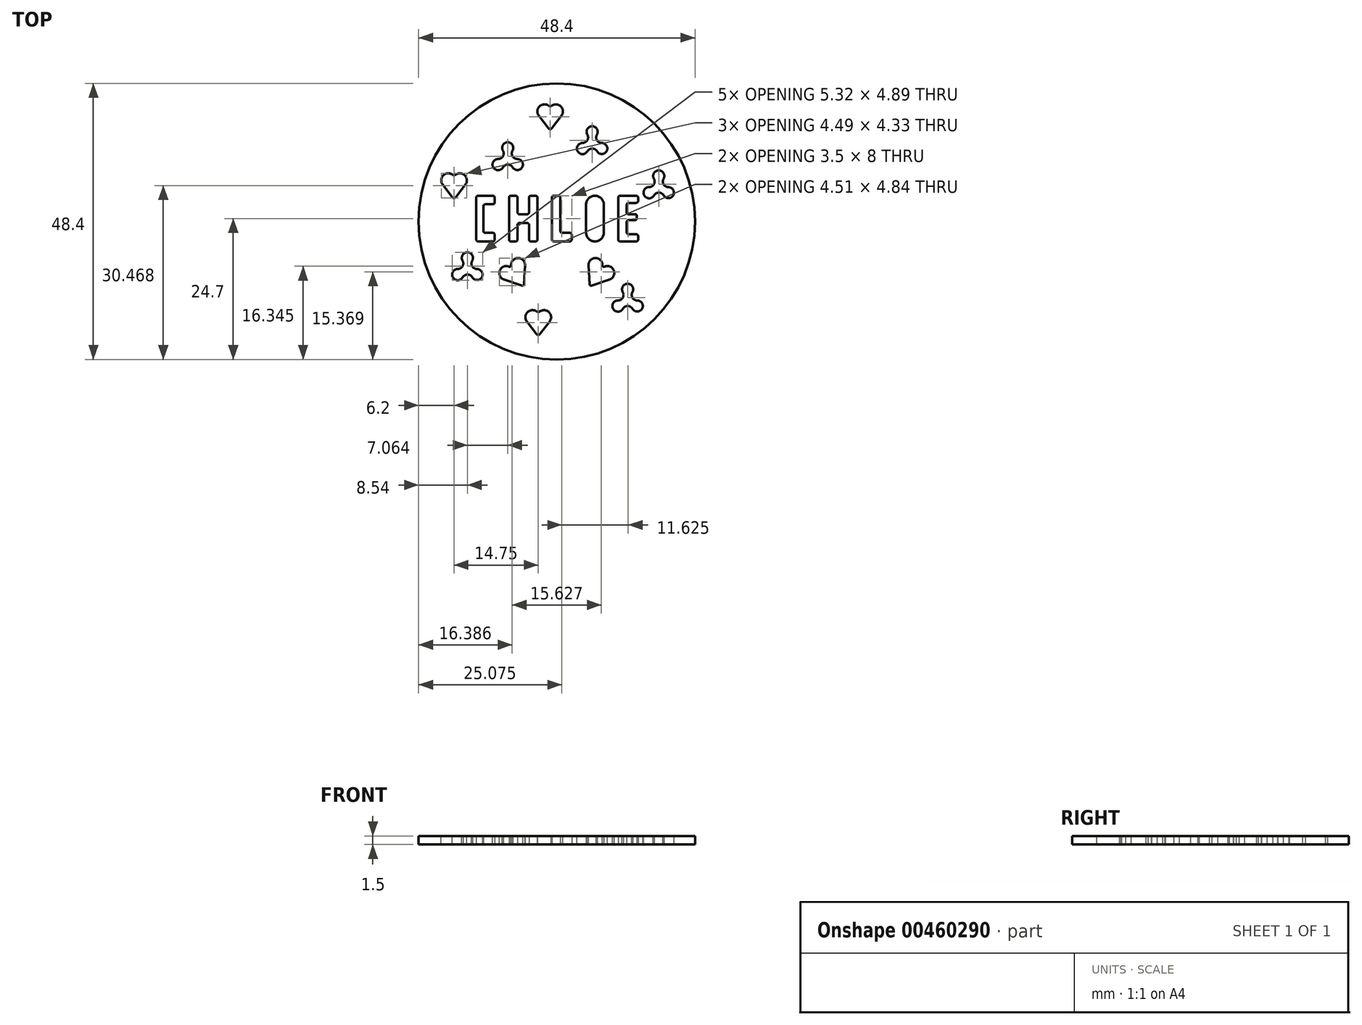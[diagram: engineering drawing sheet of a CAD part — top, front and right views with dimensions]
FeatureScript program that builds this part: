
annotation { "Feature Type Name" : "Feature", "Feature Type Description" : "" }
export const myFeature = defineFeature(function(context is Context, id is Id, definition is map)
    precondition{}
    {
        {
            var Q0;
            Q0=qCreatedBy(makeId("Top.planeOp"),FACE);
            var sketch = newSketch(context, id + "F0", { "sketchPlane" : qUnion([Q0])});
            skCircle(sketch, "E0", {"center": v(0, 0) * mm, "radius": 24.2 * mm});
            skLineSegment(sketch, "E1", {"start": v(-14.12, 4.15) * mm, "end": v(-14.12, -3.15) * mm});
            skLineSegment(sketch, "E2", {"start": v(-13.77, -3.5) * mm, "end": v(-11.22, -3.5) * mm});
            skLineSegment(sketch, "E3", {"start": v(-13.77, 4.5) * mm, "end": v(-11.22, 4.5) * mm});
            skLineSegment(sketch, "E4", {"start": v(-8.37, 4.15) * mm, "end": v(-8.37, -3.15) * mm});
            skLineSegment(sketch, "E5", {"start": v(-8.02, -3.5) * mm, "end": v(-7.22, -3.5) * mm});
            skLineSegment(sketch, "E6", {"start": v(-6.87, -3.15) * mm, "end": v(-6.87, -0.6) * mm});
            skLineSegment(sketch, "E7", {"start": v(-6.52, -0.25) * mm, "end": v(-5.22, -0.25) * mm});
            skLineSegment(sketch, "E8", {"start": v(-4.87, -0.6) * mm, "end": v(-4.87, -3.15) * mm});
            skLineSegment(sketch, "E9", {"start": v(-4.53, -3.5) * mm, "end": v(-3.73, -3.5) * mm});
            skLineSegment(sketch, "E10", {"start": v(-3.38, -3.15) * mm, "end": v(-3.38, 4.15) * mm});
            skLineSegment(sketch, "E11", {"start": v(-3.73, 4.5) * mm, "end": v(-4.52, 4.5) * mm});
            skLineSegment(sketch, "E12", {"start": v(-4.87, 4.15) * mm, "end": v(-4.87, 1.6) * mm});
            skLineSegment(sketch, "E13", {"start": v(-5.22, 1.25) * mm, "end": v(-6.52, 1.25) * mm});
            skLineSegment(sketch, "E14", {"start": v(-6.87, 1.6) * mm, "end": v(-6.87, 4.15) * mm});
            skLineSegment(sketch, "E15", {"start": v(-7.22, 4.5) * mm, "end": v(-8.02, 4.5) * mm});
            skLineSegment(sketch, "E16", {"start": v(-0.88, 4.15) * mm, "end": v(-0.87, -3.15) * mm});
            skLineSegment(sketch, "E17", {"start": v(-0.52, -3.5) * mm, "end": v(2.28, -3.5) * mm});
            skLineSegment(sketch, "E18", {"start": v(2.63, -3.15) * mm, "end": v(2.63, -2.35) * mm});
            skLineSegment(sketch, "E19", {"start": v(2.28, -2) * mm, "end": v(0.98, -2) * mm});
            skLineSegment(sketch, "E20", {"start": v(0.63, -1.65) * mm, "end": v(0.62, 4.15) * mm});
            skLineSegment(sketch, "E21", {"start": v(0.27, 4.5) * mm, "end": v(-0.53, 4.5) * mm});
            skLineSegment(sketch, "E22", {"start": v(5.12, 2.94) * mm, "end": v(5.13, -1.94) * mm});
            skLineSegment(sketch, "E23", {"start": v(8.25, 2.94) * mm, "end": v(8.25, -1.94) * mm});
            skArc(sketch, "E24", {"start": v(5.12, 2.94) * mm, "mid": v(6.69, 4.5) * mm, "end": v(8.25, 2.94) * mm});
            skArc(sketch, "E25", {"start": v(8.25, -1.94) * mm, "mid": v(6.69, -3.5) * mm, "end": v(5.12, -1.94) * mm});
            skLineSegment(sketch, "E26", {"start": v(13.9, 4.5) * mm, "end": v(11.1, 4.5) * mm});
            skLineSegment(sketch, "E27", {"start": v(10.75, 4.15) * mm, "end": v(10.75, -3.15) * mm});
            skLineSegment(sketch, "E28", {"start": v(11.1, -3.5) * mm, "end": v(13.9, -3.5) * mm});
            skLineSegment(sketch, "E29", {"start": v(14.25, -3.15) * mm, "end": v(14.25, -2.6) * mm});
            skLineSegment(sketch, "E30", {"start": v(13.9, -2.25) * mm, "end": v(12.6, -2.25) * mm});
            skLineSegment(sketch, "E31", {"start": v(12.25, -1.9) * mm, "end": v(12.25, -0.1) * mm});
            skLineSegment(sketch, "E32", {"start": v(14, 0.5) * mm, "end": v(14, 1) * mm});
            skLineSegment(sketch, "E33", {"start": v(13.75, 1.25) * mm, "end": v(12.6, 1.25) * mm});
            skLineSegment(sketch, "E34", {"start": v(12.25, 1.6) * mm, "end": v(12.25, 2.9) * mm});
            skLineSegment(sketch, "E35", {"start": v(12.6, 3.25) * mm, "end": v(13.9, 3.25) * mm});
            skLineSegment(sketch, "E36", {"start": v(14.25, 3.6) * mm, "end": v(14.25, 4.15) * mm});
            skLineSegment(sketch, "E37", {"start": v(-10.87, 4.15) * mm, "end": v(-10.87, 3.35) * mm});
            skLineSegment(sketch, "E38", {"start": v(-11.22, 3) * mm, "end": v(-12.52, 3) * mm});
            skLineSegment(sketch, "E39", {"start": v(-12.87, 2.65) * mm, "end": v(-12.87, -1.65) * mm});
            skLineSegment(sketch, "E40", {"start": v(-12.52, -2) * mm, "end": v(-11.22, -2) * mm});
            skLineSegment(sketch, "E41", {"start": v(-10.87, -2.35) * mm, "end": v(-10.87, -3.15) * mm});
            skPoint(sketch, "E42.visualSharp", {"position": v(-14.12, 4.5) * mm});
            skArc(sketch, "E42.filletArc", {"start": v(-13.77, 4.5) * mm, "mid": v(-14.02, 4.4) * mm, "end": v(-14.12, 4.15) * mm});
            skPoint(sketch, "E43.visualSharp", {"position": v(-10.87, 4.5) * mm});
            skArc(sketch, "E43.filletArc", {"start": v(-10.87, 4.15) * mm, "mid": v(-10.98, 4.4) * mm, "end": v(-11.22, 4.5) * mm});
            skPoint(sketch, "E44.visualSharp", {"position": v(-10.87, 3) * mm});
            skArc(sketch, "E44.filletArc", {"start": v(-11.22, 3) * mm, "mid": v(-10.98, 3.1) * mm, "end": v(-10.87, 3.35) * mm});
            skPoint(sketch, "E45.visualSharp", {"position": v(-12.87, 3) * mm});
            skArc(sketch, "E45.filletArc", {"start": v(-12.52, 3) * mm, "mid": v(-12.77, 2.9) * mm, "end": v(-12.87, 2.65) * mm});
            skPoint(sketch, "E46.visualSharp", {"position": v(-12.87, -2) * mm});
            skArc(sketch, "E46.filletArc", {"start": v(-12.87, -1.65) * mm, "mid": v(-12.77, -1.9) * mm, "end": v(-12.52, -2) * mm});
            skPoint(sketch, "E47.visualSharp", {"position": v(-10.87, -2) * mm});
            skArc(sketch, "E47.filletArc", {"start": v(-10.87, -2.35) * mm, "mid": v(-10.98, -2.1) * mm, "end": v(-11.22, -2) * mm});
            skPoint(sketch, "E48.visualSharp", {"position": v(-10.87, -3.5) * mm});
            skArc(sketch, "E48.filletArc", {"start": v(-11.22, -3.5) * mm, "mid": v(-10.98, -3.4) * mm, "end": v(-10.87, -3.15) * mm});
            skPoint(sketch, "E49.visualSharp", {"position": v(-14.12, -3.5) * mm});
            skArc(sketch, "E49.filletArc", {"start": v(-14.12, -3.15) * mm, "mid": v(-14.02, -3.4) * mm, "end": v(-13.77, -3.5) * mm});
            skPoint(sketch, "E50.visualSharp", {"position": v(-8.37, 4.5) * mm});
            skArc(sketch, "E50.filletArc", {"start": v(-8.02, 4.5) * mm, "mid": v(-8.27, 4.4) * mm, "end": v(-8.37, 4.15) * mm});
            skPoint(sketch, "E51.visualSharp", {"position": v(-6.87, 4.5) * mm});
            skArc(sketch, "E51.filletArc", {"start": v(-6.87, 4.15) * mm, "mid": v(-6.98, 4.4) * mm, "end": v(-7.22, 4.5) * mm});
            skPoint(sketch, "E52.visualSharp", {"position": v(-6.87, 1.25) * mm});
            skArc(sketch, "E52.filletArc", {"start": v(-6.87, 1.6) * mm, "mid": v(-6.77, 1.35) * mm, "end": v(-6.52, 1.25) * mm});
            skPoint(sketch, "E53.visualSharp", {"position": v(-4.87, 1.25) * mm});
            skArc(sketch, "E53.filletArc", {"start": v(-5.22, 1.25) * mm, "mid": v(-4.98, 1.35) * mm, "end": v(-4.87, 1.6) * mm});
            skPoint(sketch, "E54.visualSharp", {"position": v(-4.87, 4.5) * mm});
            skArc(sketch, "E54.filletArc", {"start": v(-4.52, 4.5) * mm, "mid": v(-4.77, 4.4) * mm, "end": v(-4.87, 4.15) * mm});
            skPoint(sketch, "E55.visualSharp", {"position": v(-3.38, 4.5) * mm});
            skArc(sketch, "E55.filletArc", {"start": v(-3.37, 4.15) * mm, "mid": v(-3.48, 4.4) * mm, "end": v(-3.73, 4.5) * mm});
            skPoint(sketch, "E56.visualSharp", {"position": v(-3.37, -3.5) * mm});
            skArc(sketch, "E56.filletArc", {"start": v(-3.73, -3.5) * mm, "mid": v(-3.48, -3.4) * mm, "end": v(-3.37, -3.15) * mm});
            skPoint(sketch, "E57.visualSharp", {"position": v(-4.87, -3.5) * mm});
            skArc(sketch, "E57.filletArc", {"start": v(-4.88, -3.15) * mm, "mid": v(-4.77, -3.4) * mm, "end": v(-4.53, -3.5) * mm});
            skPoint(sketch, "E58.visualSharp", {"position": v(-4.87, -0.25) * mm});
            skArc(sketch, "E58.filletArc", {"start": v(-4.87, -0.6) * mm, "mid": v(-4.98, -0.35) * mm, "end": v(-5.22, -0.25) * mm});
            skPoint(sketch, "E59.visualSharp", {"position": v(-6.87, -0.25) * mm});
            skArc(sketch, "E59.filletArc", {"start": v(-6.52, -0.25) * mm, "mid": v(-6.77, -0.35) * mm, "end": v(-6.87, -0.6) * mm});
            skPoint(sketch, "E60.visualSharp", {"position": v(-6.87, -3.5) * mm});
            skArc(sketch, "E60.filletArc", {"start": v(-7.22, -3.5) * mm, "mid": v(-6.98, -3.4) * mm, "end": v(-6.87, -3.15) * mm});
            skPoint(sketch, "E61.visualSharp", {"position": v(-8.37, -3.5) * mm});
            skArc(sketch, "E61.filletArc", {"start": v(-8.37, -3.15) * mm, "mid": v(-8.27, -3.4) * mm, "end": v(-8.02, -3.5) * mm});
            skPoint(sketch, "E62.visualSharp", {"position": v(-0.88, 4.5) * mm});
            skArc(sketch, "E62.filletArc", {"start": v(-0.53, 4.5) * mm, "mid": v(-0.77, 4.4) * mm, "end": v(-0.88, 4.15) * mm});
            skPoint(sketch, "E63.visualSharp", {"position": v(0.62, 4.5) * mm});
            skArc(sketch, "E63.filletArc", {"start": v(0.62, 4.15) * mm, "mid": v(0.52, 4.4) * mm, "end": v(0.27, 4.5) * mm});
            skPoint(sketch, "E64.visualSharp", {"position": v(0.63, -2) * mm});
            skArc(sketch, "E64.filletArc", {"start": v(0.63, -1.65) * mm, "mid": v(0.73, -1.9) * mm, "end": v(0.98, -2) * mm});
            skPoint(sketch, "E65.visualSharp", {"position": v(2.63, -2) * mm});
            skArc(sketch, "E65.filletArc", {"start": v(2.63, -2.35) * mm, "mid": v(2.52, -2.1) * mm, "end": v(2.28, -2) * mm});
            skPoint(sketch, "E66.visualSharp", {"position": v(2.63, -3.5) * mm});
            skArc(sketch, "E66.filletArc", {"start": v(2.28, -3.5) * mm, "mid": v(2.52, -3.4) * mm, "end": v(2.63, -3.15) * mm});
            skPoint(sketch, "E67.visualSharp", {"position": v(-0.87, -3.5) * mm});
            skArc(sketch, "E67.filletArc", {"start": v(-0.87, -3.15) * mm, "mid": v(-0.77, -3.4) * mm, "end": v(-0.52, -3.5) * mm});
            skPoint(sketch, "E68.visualSharp", {"position": v(14.25, -3.5) * mm});
            skArc(sketch, "E68.filletArc", {"start": v(13.9, -3.5) * mm, "mid": v(14.15, -3.4) * mm, "end": v(14.25, -3.15) * mm});
            skPoint(sketch, "E69.visualSharp", {"position": v(14.25, -2.25) * mm});
            skArc(sketch, "E69.filletArc", {"start": v(14.25, -2.6) * mm, "mid": v(14.15, -2.35) * mm, "end": v(13.9, -2.25) * mm});
            skPoint(sketch, "E70.visualSharp", {"position": v(12.25, -2.25) * mm});
            skArc(sketch, "E70.filletArc", {"start": v(12.25, -1.9) * mm, "mid": v(12.35, -2.15) * mm, "end": v(12.6, -2.25) * mm});
            skPoint(sketch, "E71.visualSharp", {"position": v(12.25, 0) * mm});
            skArc(sketch, "E71.filletArc", {"start": v(12.6, 0.25) * mm, "mid": v(12.35, 0.15) * mm, "end": v(12.25, -0.1) * mm});
            skPoint(sketch, "E72.visualSharp", {"position": v(10.75, -3.5) * mm});
            skArc(sketch, "E72.filletArc", {"start": v(10.75, -3.15) * mm, "mid": v(10.85, -3.4) * mm, "end": v(11.1, -3.5) * mm});
            skPoint(sketch, "E73.visualSharp", {"position": v(10.75, 4.5) * mm});
            skArc(sketch, "E73.filletArc", {"start": v(11.1, 4.5) * mm, "mid": v(10.85, 4.4) * mm, "end": v(10.75, 4.15) * mm});
            skPoint(sketch, "E74.visualSharp", {"position": v(14.25, 4.5) * mm});
            skArc(sketch, "E74.filletArc", {"start": v(14.25, 4.15) * mm, "mid": v(14.15, 4.4) * mm, "end": v(13.9, 4.5) * mm});
            skPoint(sketch, "E75.visualSharp", {"position": v(14.25, 3.25) * mm});
            skArc(sketch, "E75.filletArc", {"start": v(13.9, 3.25) * mm, "mid": v(14.15, 3.35) * mm, "end": v(14.25, 3.6) * mm});
            skPoint(sketch, "E76.visualSharp", {"position": v(12.25, 3.25) * mm});
            skArc(sketch, "E76.filletArc", {"start": v(12.6, 3.25) * mm, "mid": v(12.35, 3.15) * mm, "end": v(12.25, 2.9) * mm});
            skPoint(sketch, "E77.visualSharp", {"position": v(12.25, 1.25) * mm});
            skArc(sketch, "E77.filletArc", {"start": v(12.25, 1.6) * mm, "mid": v(12.35, 1.35) * mm, "end": v(12.6, 1.25) * mm});
            skPoint(sketch, "E78.visualSharp", {"position": v(14, 1.25) * mm});
            skArc(sketch, "E78.filletArc", {"start": v(14, 1) * mm, "mid": v(13.93, 1.18) * mm, "end": v(13.75, 1.25) * mm});
            skArc(sketch, "E79.filletArc", {"start": v(13.75, 0.25) * mm, "mid": v(13.93, 0.32) * mm, "end": v(14, 0.5) * mm});
            skLineSegment(sketch, "E80", {"start": v(13.75, 0.25) * mm, "end": v(12.6, 0.25) * mm});
            skSolve(sketch);
        }
        {
            var Q0;
            Q0 = qSketchRegion(id + "F0", true);
            extrude(context, id + "F1", {"entities" : qUnion([Q0]), "depth" : 1.5 * mm});
        }
        {
            var Q0;
            Q0=makeQuery(id+"F1.opExtrude","CAP_FACE",FACE,{"disambiguationData":[OSD([sQuery(id+"F0.wireOp",EDGE,"E0"),sQuery(id+"F0.wireOp",EDGE,"E1"),sQuery(id+"F0.wireOp",EDGE,"E2"),sQuery(id+"F0.wireOp",EDGE,"E3"),sQuery(id+"F0.wireOp",EDGE,"E4"),sQuery(id+"F0.wireOp",EDGE,"E5"),sQuery(id+"F0.wireOp",EDGE,"E6"),sQuery(id+"F0.wireOp",EDGE,"E7"),sQuery(id+"F0.wireOp",EDGE,"E8"),sQuery(id+"F0.wireOp",EDGE,"E9"),sQuery(id+"F0.wireOp",EDGE,"E10"),sQuery(id+"F0.wireOp",EDGE,"E11"),sQuery(id+"F0.wireOp",EDGE,"E12"),sQuery(id+"F0.wireOp",EDGE,"E13"),sQuery(id+"F0.wireOp",EDGE,"E14"),sQuery(id+"F0.wireOp",EDGE,"E15"),sQuery(id+"F0.wireOp",EDGE,"E16"),sQuery(id+"F0.wireOp",EDGE,"E17"),sQuery(id+"F0.wireOp",EDGE,"E18"),sQuery(id+"F0.wireOp",EDGE,"E19"),sQuery(id+"F0.wireOp",EDGE,"E20"),sQuery(id+"F0.wireOp",EDGE,"E21"),sQuery(id+"F0.wireOp",EDGE,"E22"),sQuery(id+"F0.wireOp",EDGE,"E23"),sQuery(id+"F0.wireOp",EDGE,"E24"),sQuery(id+"F0.wireOp",EDGE,"E25"),sQuery(id+"F0.wireOp",EDGE,"E26"),sQuery(id+"F0.wireOp",EDGE,"E27"),sQuery(id+"F0.wireOp",EDGE,"E28"),sQuery(id+"F0.wireOp",EDGE,"E29"),sQuery(id+"F0.wireOp",EDGE,"E30"),sQuery(id+"F0.wireOp",EDGE,"E31"),sQuery(id+"F0.wireOp",EDGE,"e08n0Kjc-3YKp-OetY-h4IO-rFLRSXg9Mj5R"),sQuery(id+"F0.wireOp",EDGE,"E32"),sQuery(id+"F0.wireOp",EDGE,"E33"),sQuery(id+"F0.wireOp",EDGE,"E34"),sQuery(id+"F0.wireOp",EDGE,"E35"),sQuery(id+"F0.wireOp",EDGE,"E36"),sQuery(id+"F0.wireOp",EDGE,"E37"),sQuery(id+"F0.wireOp",EDGE,"E38"),sQuery(id+"F0.wireOp",EDGE,"E39"),sQuery(id+"F0.wireOp",EDGE,"E40"),sQuery(id+"F0.wireOp",EDGE,"E41"),sQuery(id+"F0.wireOp",EDGE,"E42.filletArc"),sQuery(id+"F0.wireOp",EDGE,"E43.filletArc"),sQuery(id+"F0.wireOp",EDGE,"E44.filletArc"),sQuery(id+"F0.wireOp",EDGE,"E45.filletArc"),sQuery(id+"F0.wireOp",EDGE,"E46.filletArc"),sQuery(id+"F0.wireOp",EDGE,"E47.filletArc"),sQuery(id+"F0.wireOp",EDGE,"E48.filletArc"),sQuery(id+"F0.wireOp",EDGE,"E49.filletArc"),sQuery(id+"F0.wireOp",EDGE,"E50.filletArc"),sQuery(id+"F0.wireOp",EDGE,"E51.filletArc"),sQuery(id+"F0.wireOp",EDGE,"E52.filletArc"),sQuery(id+"F0.wireOp",EDGE,"E53.filletArc"),sQuery(id+"F0.wireOp",EDGE,"E54.filletArc"),sQuery(id+"F0.wireOp",EDGE,"E55.filletArc"),sQuery(id+"F0.wireOp",EDGE,"E56.filletArc"),sQuery(id+"F0.wireOp",EDGE,"E57.filletArc"),sQuery(id+"F0.wireOp",EDGE,"E58.filletArc"),sQuery(id+"F0.wireOp",EDGE,"E59.filletArc"),sQuery(id+"F0.wireOp",EDGE,"E60.filletArc"),sQuery(id+"F0.wireOp",EDGE,"E61.filletArc"),sQuery(id+"F0.wireOp",EDGE,"E62.filletArc"),sQuery(id+"F0.wireOp",EDGE,"E63.filletArc"),sQuery(id+"F0.wireOp",EDGE,"E64.filletArc"),sQuery(id+"F0.wireOp",EDGE,"E65.filletArc"),sQuery(id+"F0.wireOp",EDGE,"E66.filletArc"),sQuery(id+"F0.wireOp",EDGE,"E67.filletArc"),sQuery(id+"F0.wireOp",EDGE,"E68.filletArc"),sQuery(id+"F0.wireOp",EDGE,"E69.filletArc"),sQuery(id+"F0.wireOp",EDGE,"E70.filletArc"),sQuery(id+"F0.wireOp",EDGE,"E71.filletArc"),sQuery(id+"F0.wireOp",EDGE,"E72.filletArc"),sQuery(id+"F0.wireOp",EDGE,"E73.filletArc"),sQuery(id+"F0.wireOp",EDGE,"E74.filletArc"),sQuery(id+"F0.wireOp",EDGE,"E75.filletArc"),sQuery(id+"F0.wireOp",EDGE,"E76.filletArc"),sQuery(id+"F0.wireOp",EDGE,"E77.filletArc"),sQuery(id+"F0.wireOp",EDGE,"E78.filletArc"),sQuery(id+"F0.wireOp",EDGE,"E79.filletArc")])],"isStart":false});
            var sketch = newSketch(context, id + "F2", { "sketchPlane" : qUnion([Q0])});
            skPoint(sketch, "E81.0.midPoint", {"position": v(-7.75, 12.41) * mm});
            skPoint(sketch, "E82.endSnap0", {"position": v(-9.44, 12.4) * mm});
            skPoint(sketch, "E83.endSnap0", {"position": v(-6.9, 10.95) * mm});
            skArc(sketch, "E84", {"start": v(-9.44, 12.4) * mm, "mid": v(-8.6, 13.87) * mm, "end": v(-7.75, 12.41) * mm});
            skArc(sketch, "E85", {"start": v(-6.9, 10.93) * mm, "mid": v(-6.06, 9.49) * mm, "end": v(-7.73, 9.48) * mm});
            skArc(sketch, "E86", {"start": v(-9.42, 9.47) * mm, "mid": v(-11.12, 9.47) * mm, "end": v(-10.27, 10.94) * mm});
            skArc(sketch, "E87", {"start": v(-10.27, 10.94) * mm, "mid": v(-9.43, 11.43) * mm, "end": v(-9.44, 12.4) * mm});
            skArc(sketch, "E88", {"start": v(-7.73, 9.48) * mm, "mid": v(-8.58, 9.97) * mm, "end": v(-9.42, 9.47) * mm});
            skArc(sketch, "E89", {"start": v(-7.75, 12.41) * mm, "mid": v(-7.75, 11.43) * mm, "end": v(-6.9, 10.93) * mm});
            skPoint(sketch, "E90.0.midPoint", {"position": v(7.04, 15.22) * mm});
            skPoint(sketch, "E91.endSnap0", {"position": v(5.35, 15.21) * mm});
            skPoint(sketch, "E92.endSnap0", {"position": v(7.9, 13.76) * mm});
            skArc(sketch, "E93", {"start": v(5.35, 15.21) * mm, "mid": v(6.18, 16.68) * mm, "end": v(7.04, 15.22) * mm});
            skArc(sketch, "E94", {"start": v(7.9, 13.74) * mm, "mid": v(8.72, 12.3) * mm, "end": v(7.05, 12.3) * mm});
            skArc(sketch, "E95", {"start": v(5.36, 12.28) * mm, "mid": v(3.66, 12.28) * mm, "end": v(4.51, 13.75) * mm});
            skArc(sketch, "E96", {"start": v(4.51, 13.75) * mm, "mid": v(5.35, 14.24) * mm, "end": v(5.35, 15.21) * mm});
            skArc(sketch, "E97", {"start": v(7.05, 12.3) * mm, "mid": v(6.2, 12.78) * mm, "end": v(5.36, 12.28) * mm});
            skArc(sketch, "E98", {"start": v(7.04, 15.22) * mm, "mid": v(7.04, 14.24) * mm, "end": v(7.9, 13.74) * mm});
            skPoint(sketch, "E99.0.midPoint", {"position": v(13.25, -12.38) * mm});
            skPoint(sketch, "E100.endSnap0", {"position": v(11.56, -12.39) * mm});
            skPoint(sketch, "E101.endSnap0", {"position": v(14.1, -13.84) * mm});
            skArc(sketch, "E102", {"start": v(11.56, -12.39) * mm, "mid": v(12.4, -10.92) * mm, "end": v(13.25, -12.38) * mm});
            skArc(sketch, "E103", {"start": v(14.1, -13.86) * mm, "mid": v(14.93, -15.3) * mm, "end": v(13.27, -15.3) * mm});
            skArc(sketch, "E104", {"start": v(11.58, -15.32) * mm, "mid": v(9.87, -15.32) * mm, "end": v(10.72, -13.85) * mm});
            skArc(sketch, "E105", {"start": v(10.72, -13.85) * mm, "mid": v(11.56, -13.36) * mm, "end": v(11.56, -12.39) * mm});
            skArc(sketch, "E106", {"start": v(13.27, -15.3) * mm, "mid": v(12.42, -14.82) * mm, "end": v(11.58, -15.32) * mm});
            skArc(sketch, "E107", {"start": v(13.25, -12.38) * mm, "mid": v(13.25, -13.36) * mm, "end": v(14.1, -13.86) * mm});
            skPoint(sketch, "E108.0.midPoint", {"position": v(-14.81, -6.87) * mm});
            skPoint(sketch, "E109.endSnap0", {"position": v(-16.5, -6.88) * mm});
            skPoint(sketch, "E110.endSnap0", {"position": v(-13.96, -8.33) * mm});
            skArc(sketch, "E111", {"start": v(-16.5, -6.88) * mm, "mid": v(-15.67, -5.4) * mm, "end": v(-14.81, -6.87) * mm});
            skArc(sketch, "E112", {"start": v(-13.96, -8.35) * mm, "mid": v(-13.13, -9.8) * mm, "end": v(-14.8, -9.8) * mm});
            skArc(sketch, "E113", {"start": v(-16.49, -9.8) * mm, "mid": v(-18.19, -9.81) * mm, "end": v(-17.34, -8.34) * mm});
            skArc(sketch, "E114", {"start": v(-17.34, -8.34) * mm, "mid": v(-16.5, -7.85) * mm, "end": v(-16.5, -6.88) * mm});
            skArc(sketch, "E115", {"start": v(-14.8, -9.8) * mm, "mid": v(-15.64, -9.31) * mm, "end": v(-16.49, -9.8) * mm});
            skArc(sketch, "E116", {"start": v(-14.81, -6.87) * mm, "mid": v(-14.8, -7.85) * mm, "end": v(-13.96, -8.35) * mm});
            skPoint(sketch, "E117.0.midPoint", {"position": v(18.7, 7.49) * mm});
            skPoint(sketch, "E118.endSnap0", {"position": v(17.01, 7.48) * mm});
            skPoint(sketch, "E119.endSnap0", {"position": v(19.55, 6.03) * mm});
            skArc(sketch, "E120", {"start": v(17.01, 7.48) * mm, "mid": v(17.85, 8.95) * mm, "end": v(18.7, 7.49) * mm});
            skArc(sketch, "E121", {"start": v(19.55, 6) * mm, "mid": v(20.39, 4.56) * mm, "end": v(18.72, 4.56) * mm});
            skArc(sketch, "E122", {"start": v(17.03, 4.55) * mm, "mid": v(15.33, 4.54) * mm, "end": v(16.17, 6.02) * mm});
            skArc(sketch, "E123", {"start": v(16.17, 6.02) * mm, "mid": v(17.02, 6.5) * mm, "end": v(17.01, 7.48) * mm});
            skArc(sketch, "E124", {"start": v(18.72, 4.56) * mm, "mid": v(17.87, 5.04) * mm, "end": v(17.03, 4.55) * mm});
            skArc(sketch, "E125", {"start": v(18.7, 7.49) * mm, "mid": v(18.7, 6.5) * mm, "end": v(19.55, 6) * mm});
            skLineSegment(sketch, "E126", {"start": v(6.08, -11.24) * mm, "end": v(9.23, -10.2) * mm});
            skArc(sketch, "E127", {"start": v(9.23, -10.2) * mm, "mid": v(9.99, -8.6) * mm, "end": v(8.35, -7.92) * mm});
            skArc(sketch, "E128.MirrorCS", {"start": v(5.56, -7.7) * mm, "mid": v(6.77, -6.41) * mm, "end": v(8, -7.69) * mm});
            skLineSegment(sketch, "E129.MirrorCS", {"start": v(5.75, -11.01) * mm, "end": v(5.56, -7.7) * mm});
            skArc(sketch, "E130.filletArc", {"start": v(5.75, -11.01) * mm, "mid": v(5.86, -11.2) * mm, "end": v(6.08, -11.24) * mm});
            skArc(sketch, "E131.filletArc", {"start": v(8, -7.69) * mm, "mid": v(8.11, -7.9) * mm, "end": v(8.35, -7.92) * mm});
            skLineSegment(sketch, "E132", {"start": v(-17.68, 4.26) * mm, "end": v(-16.01, 6.43) * mm});
            skArc(sketch, "E133", {"start": v(-16.01, 6.43) * mm, "mid": v(-16.11, 8.07) * mm, "end": v(-17.76, 8.18) * mm});
            skArc(sketch, "E134.MirrorCS", {"start": v(-19.99, 6.43) * mm, "mid": v(-19.89, 8.07) * mm, "end": v(-18.24, 8.18) * mm});
            skLineSegment(sketch, "E135.MirrorCS", {"start": v(-18.32, 4.26) * mm, "end": v(-19.99, 6.43) * mm});
            skArc(sketch, "E136.filletArc", {"start": v(-18.32, 4.26) * mm, "mid": v(-18, 4.1) * mm, "end": v(-17.68, 4.26) * mm});
            skArc(sketch, "E137.filletArc", {"start": v(-18.24, 8.18) * mm, "mid": v(-18, 8.1) * mm, "end": v(-17.76, 8.18) * mm});
            skArc(sketch, "E138.MirrorCS", {"start": v(-8, -7.69) * mm, "mid": v(-8.11, -7.9) * mm, "end": v(-8.35, -7.92) * mm});
            skArc(sketch, "E139.MirrorCS", {"start": v(-5.75, -11.01) * mm, "mid": v(-5.86, -11.2) * mm, "end": v(-6.08, -11.24) * mm});
            skLineSegment(sketch, "E140.MirrorCS", {"start": v(-5.75, -11.01) * mm, "end": v(-5.56, -7.7) * mm});
            skArc(sketch, "E141.MirrorCS", {"start": v(-9.23, -10.2) * mm, "mid": v(-9.99, -8.6) * mm, "end": v(-8.35, -7.92) * mm});
            skLineSegment(sketch, "E142.MirrorCS", {"start": v(-6.08, -11.24) * mm, "end": v(-9.23, -10.2) * mm});
            skArc(sketch, "E143.MirrorCS", {"start": v(-5.56, -7.7) * mm, "mid": v(-6.77, -6.41) * mm, "end": v(-8, -7.69) * mm});
            skLineSegment(sketch, "E144", {"start": v(-0.85, 16.34) * mm, "end": v(0.82, 18.51) * mm});
            skArc(sketch, "E145", {"start": v(0.82, 18.51) * mm, "mid": v(0.72, 20.15) * mm, "end": v(-0.92, 20.27) * mm});
            skArc(sketch, "E146.MirrorCS", {"start": v(-3.15, 18.51) * mm, "mid": v(-3.05, 20.15) * mm, "end": v(-1.4, 20.27) * mm});
            skLineSegment(sketch, "E147.MirrorCS", {"start": v(-1.48, 16.34) * mm, "end": v(-3.15, 18.51) * mm});
            skArc(sketch, "E148.filletArc", {"start": v(-1.48, 16.34) * mm, "mid": v(-1.16, 16.19) * mm, "end": v(-0.85, 16.34) * mm});
            skArc(sketch, "E149.filletArc", {"start": v(-1.4, 20.27) * mm, "mid": v(-1.16, 20.19) * mm, "end": v(-0.92, 20.27) * mm});
            skLineSegment(sketch, "E150", {"start": v(-2.93, -19.73) * mm, "end": v(-1.26, -17.56) * mm});
            skArc(sketch, "E151", {"start": v(-1.26, -17.56) * mm, "mid": v(-1.36, -15.91) * mm, "end": v(-3, -15.8) * mm});
            skArc(sketch, "E152.MirrorCS", {"start": v(-5.24, -17.56) * mm, "mid": v(-5.14, -15.91) * mm, "end": v(-3.5, -15.8) * mm});
            skLineSegment(sketch, "E153.MirrorCS", {"start": v(-3.57, -19.73) * mm, "end": v(-5.24, -17.56) * mm});
            skArc(sketch, "E154.filletArc", {"start": v(-3.57, -19.73) * mm, "mid": v(-3.25, -19.88) * mm, "end": v(-2.93, -19.73) * mm});
            skArc(sketch, "E155.filletArc", {"start": v(-3.5, -15.8) * mm, "mid": v(-3.25, -15.88) * mm, "end": v(-3, -15.8) * mm});
            skSolve(sketch);
        }
        {
            var Q0;
            Q0 = qSketchRegion(id + "F2", true);
            extrude(context, id + "F3", {"entities" : qUnion([Q0]), "operationType" : NewBodyOperationType.REMOVE, "endBound" : BoundingType.THROUGH_ALL, "oppositeDirection" : true, "depth" : 25 * mm});
        }
    });
